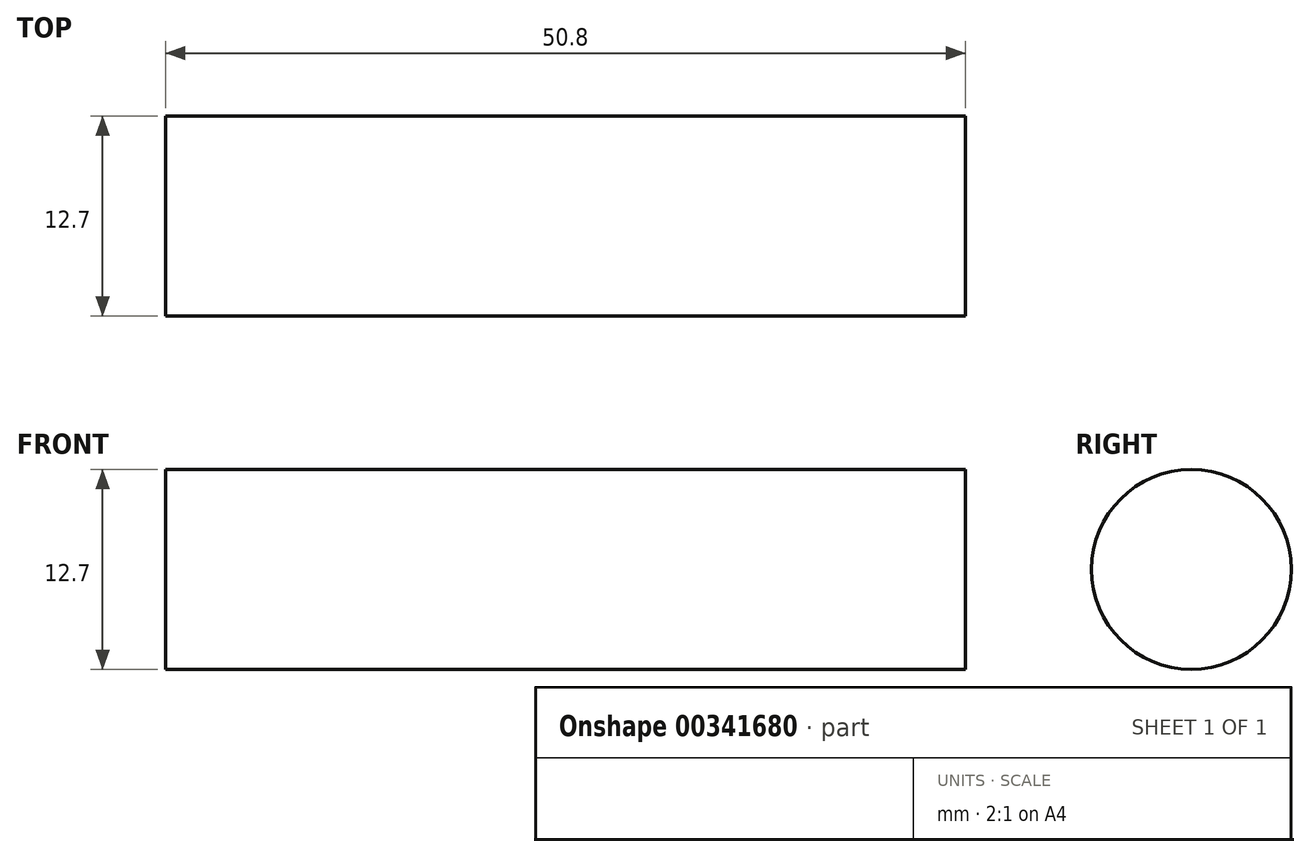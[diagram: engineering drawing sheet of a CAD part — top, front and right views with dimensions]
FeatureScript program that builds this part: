
annotation { "Feature Type Name" : "Feature", "Feature Type Description" : "" }
export const myFeature = defineFeature(function(context is Context, id is Id, definition is map)
    precondition{}
    {
        {
            var Q0;
            Q0=qCreatedBy(makeId("Right.planeOp"),FACE);
            var sketch = newSketch(context, id + "F0", { "sketchPlane" : qUnion([Q0])});
            skCircle(sketch, "E0", {"center": v(-29.93, 33.67) * mm, "radius": 6.35 * mm});
            skSolve(sketch);
        }
        {
            var Q0;
            Q0=makeQuery(id+"F0.imprint","IMPRINT",FACE,{"disambiguationData":[TD([[makeQuery(id+"F0.imprint","IMPRINT",EDGE,{"derivedFrom":sQuery(id+"F0.wireOp",EDGE,"E0")}),1.0]])]});
            extrude(context, id + "F1", {"entities" : qUnion([Q0]), "depth" : 50.8 * mm, "offsetDistance" : 25.4 * mm});
        }
    });
